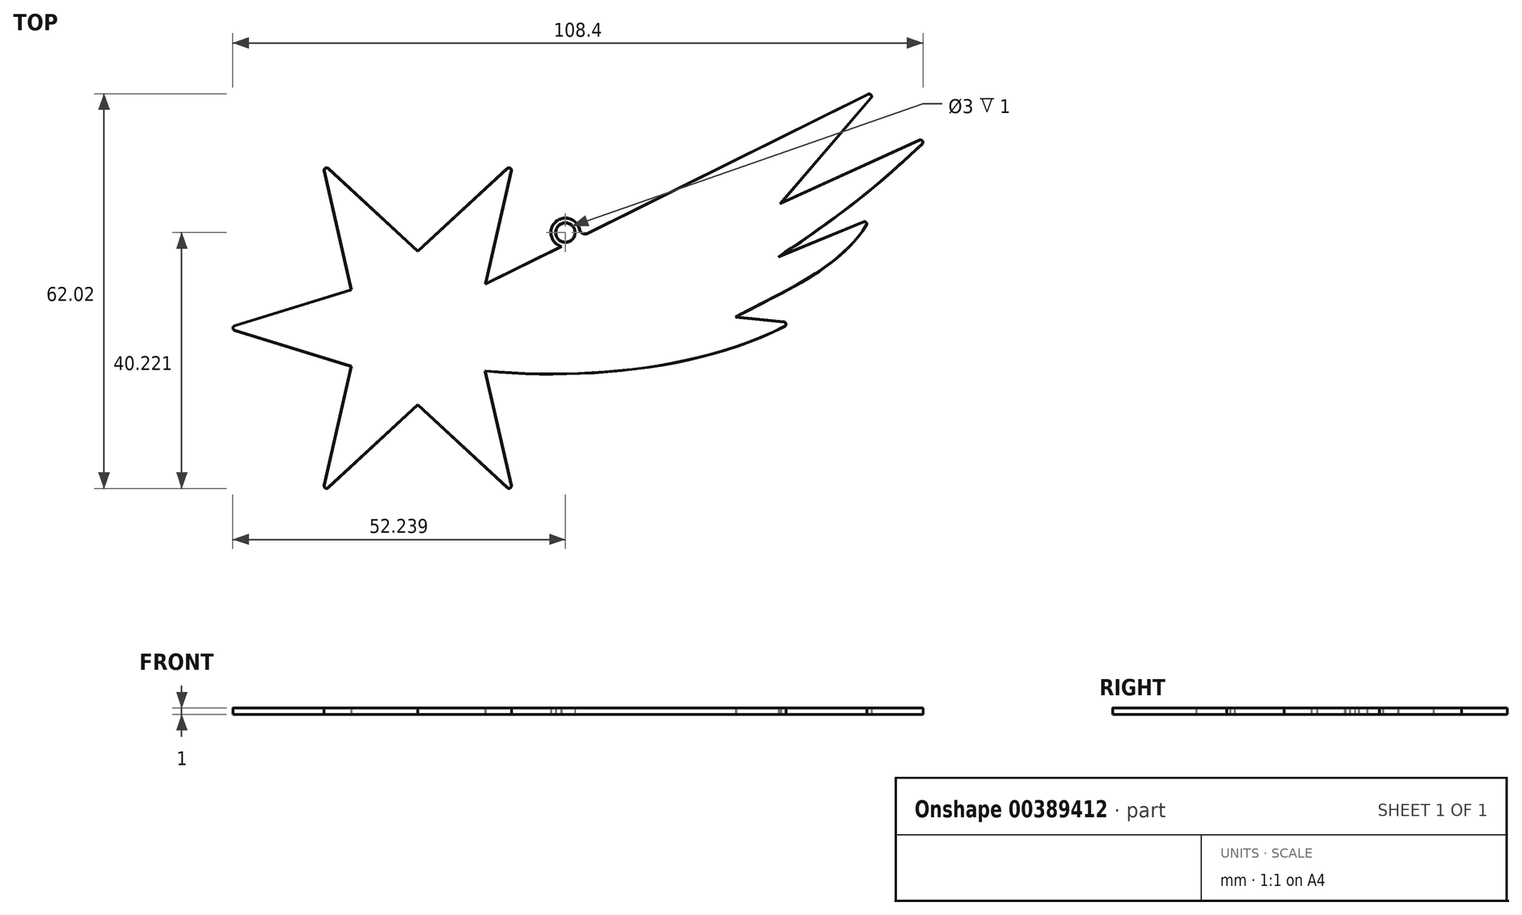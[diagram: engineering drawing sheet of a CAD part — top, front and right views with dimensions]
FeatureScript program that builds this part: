
annotation { "Feature Type Name" : "Feature", "Feature Type Description" : "" }
export const myFeature = defineFeature(function(context is Context, id is Id, definition is map)
    precondition{}
    {
        {
            var Q0;
            Q0=qCreatedBy(makeId("Top.planeOp"),FACE);
            var sketch = newSketch(context, id + "F0", { "sketchPlane" : qUnion([Q0])});
            skCircle(sketch, "E0.cCircle", {"center": v(0, 0) * mm, "radius": 30 * mm, "construction": true});
            skLineSegment(sketch, "E0.0", {"start": v(-30, 0) * mm, "end": v(-15, 25.98) * mm, "construction": true});
            skLineSegment(sketch, "E0.1", {"start": v(-15, 25.98) * mm, "end": v(15, 25.98) * mm, "construction": true});
            skLineSegment(sketch, "E0.2", {"start": v(15, 25.98) * mm, "end": v(30, 0) * mm, "construction": true});
            skLineSegment(sketch, "E0.3", {"start": v(30, 0) * mm, "end": v(15, -25.98) * mm, "construction": true});
            skLineSegment(sketch, "E0.4", {"start": v(15, -25.98) * mm, "end": v(-15, -25.98) * mm, "construction": true});
            skLineSegment(sketch, "E0.5", {"start": v(-15, -25.98) * mm, "end": v(-30, 0) * mm, "construction": true});
            skCircle(sketch, "E1.cCircle", {"center": v(0, 0) * mm, "radius": 12.09 * mm, "construction": true});
            skLineSegment(sketch, "E1.0", {"start": v(0, 12.09) * mm, "end": v(10.47, 6.04) * mm, "construction": true});
            skLineSegment(sketch, "E1.1", {"start": v(10.47, 6.04) * mm, "end": v(10.47, -6.04) * mm, "construction": true});
            skLineSegment(sketch, "E1.2", {"start": v(10.47, -6.04) * mm, "end": v(0, -12.09) * mm, "construction": true});
            skLineSegment(sketch, "E1.3", {"start": v(0, -12.09) * mm, "end": v(-10.47, -6.04) * mm, "construction": true});
            skLineSegment(sketch, "E1.4", {"start": v(-10.47, -6.04) * mm, "end": v(-10.47, 6.04) * mm, "construction": true});
            skLineSegment(sketch, "E1.5", {"start": v(-10.47, 6.04) * mm, "end": v(0, 12.09) * mm, "construction": true});
            skLineSegment(sketch, "E2", {"start": v(-15, 25.98) * mm, "end": v(-10.47, 6.04) * mm});
            skLineSegment(sketch, "E3", {"start": v(-30, 0) * mm, "end": v(-10.47, 6.04) * mm});
            skLineSegment(sketch, "E4", {"start": v(-30, 0) * mm, "end": v(-10.47, -6.04) * mm});
            skLineSegment(sketch, "E5", {"start": v(-10.47, -6.04) * mm, "end": v(-15, -25.98) * mm});
            skLineSegment(sketch, "E6", {"start": v(-15, -25.98) * mm, "end": v(0, -12.09) * mm});
            skLineSegment(sketch, "E7", {"start": v(0, -12.09) * mm, "end": v(15, -25.98) * mm});
            skLineSegment(sketch, "E8", {"start": v(15, -25.98) * mm, "end": v(10.47, -6.04) * mm});
            skLineSegment(sketch, "E9", {"start": v(10.47, -6.04) * mm, "end": v(30, 0) * mm});
            skLineSegment(sketch, "E10", {"start": v(30, 0) * mm, "end": v(10.47, 6.04) * mm});
            skLineSegment(sketch, "E11", {"start": v(10.47, 6.04) * mm, "end": v(15, 25.98) * mm});
            skLineSegment(sketch, "E12", {"start": v(15, 25.98) * mm, "end": v(0, 12.09) * mm});
            skLineSegment(sketch, "E13", {"start": v(0, 12.09) * mm, "end": v(-15, 25.98) * mm});
            skSolve(sketch);
        }
        {
            var Q0;
            Q0=qCreatedBy(makeId("Top.planeOp"),FACE);
            var sketch = newSketch(context, id + "F1", { "sketchPlane" : qUnion([Q0])});
            skLineSegment(sketch, "E14", {"start": v(7.39, 5.35) * mm, "end": v(72.49, 37.65) * mm});
            skFitSpline(sketch, "E15", {"points": [v(72.49, 37.65) * mm, v(57.07, 19.7) * mm], "startDerivative": vector(-15.42, -17.95) * mm, "endDerivative": vector(-15.42, -17.95) * mm});
            skFitSpline(sketch, "E16", {"points": [v(57.07, 19.7) * mm, v(80.89, 30.51) * mm], "startDerivative": vector(23.81, 10.81) * mm, "endDerivative": vector(23.81, 10.81) * mm});
            skFitSpline(sketch, "E17", {"points": [v(80.89, 30.51) * mm, v(57.07, 11.41) * mm], "startDerivative": vector(-25.7, -25.23) * mm, "endDerivative": vector(-26.86, -18.25) * mm});
            skFitSpline(sketch, "E18", {"points": [v(57.07, 11.41) * mm, v(71.1, 17.17) * mm], "startDerivative": vector(14.04, 5.75) * mm, "endDerivative": vector(14.04, 5.75) * mm});
            skFitSpline(sketch, "E19", {"points": [v(71.1, 17.17) * mm, v(50.05, 1.75) * mm], "startDerivative": vector(-12.49, -22.5) * mm, "endDerivative": vector(-25.34, -13.6) * mm});
            skFitSpline(sketch, "E20", {"points": [v(50.05, 1.75) * mm, v(58.82, 0.86) * mm], "startDerivative": vector(8.76, -0.9) * mm, "endDerivative": vector(8.76, -0.9) * mm});
            skFitSpline(sketch, "E21", {"points": [v(58.82, 0.86) * mm, v(7.78, -6.48) * mm], "startDerivative": vector(-41.96, -22.87) * mm, "endDerivative": vector(-51.14, 5.99) * mm});
            skLineSegment(sketch, "E22", {"start": v(7.78, -6.48) * mm, "end": v(7.39, 5.35) * mm});
            skSolve(sketch);
        }
        {
            var Q0;
            Q0=makeQuery(id+"F0.imprint","IMPRINT",FACE,{"disambiguationData":[TD([[makeQuery(id+"F0.imprint","IMPRINT",EDGE,{"derivedFrom":sQuery(id+"F0.wireOp",EDGE,"E2")}),1.0]])]});
            extrude(context, id + "F2", {"entities" : qUnion([Q0]), "depth" : 1 * mm});
        }
        {
            var Q0;
            Q0=qSketchRegion(id+"F1",true);
            extrude(context, id + "F3", {"entities" : qUnion([Q0]), "operationType" : NewBodyOperationType.ADD, "depth" : 1 * mm});
        }
        {
            var Q0;
            Q0=makeQuery(id+"F3.boolean.opBoolean","MERGE",FACE,{"derivedFrom":[makeQuery(id+"F2.opExtrude","CAP_FACE",FACE,{"disambiguationData":[OSD([sQuery(id+"F0.wireOp",EDGE,"E2"),sQuery(id+"F0.wireOp",EDGE,"E3"),sQuery(id+"F0.wireOp",EDGE,"E4"),sQuery(id+"F0.wireOp",EDGE,"E5"),sQuery(id+"F0.wireOp",EDGE,"E6"),sQuery(id+"F0.wireOp",EDGE,"E7"),sQuery(id+"F0.wireOp",EDGE,"E8"),sQuery(id+"F0.wireOp",EDGE,"E9"),sQuery(id+"F0.wireOp",EDGE,"E10"),sQuery(id+"F0.wireOp",EDGE,"E11"),sQuery(id+"F0.wireOp",EDGE,"E12"),sQuery(id+"F0.wireOp",EDGE,"E13")])],"isStart":true}),makeQuery(id+"F3.opExtrude","CAP_FACE",FACE,{"disambiguationData":[OSD([sQuery(id+"F1.wireOp",EDGE,"E14"),sQuery(id+"F1.wireOp",EDGE,"E15"),sQuery(id+"F1.wireOp",EDGE,"E16"),sQuery(id+"F1.wireOp",EDGE,"E17"),sQuery(id+"F1.wireOp",EDGE,"E18"),sQuery(id+"F1.wireOp",EDGE,"E19"),sQuery(id+"F1.wireOp",EDGE,"E20"),sQuery(id+"F1.wireOp",EDGE,"E21"),sQuery(id+"F1.wireOp",EDGE,"E22")])],"isStart":true})]});
            var sketch = newSketch(context, id + "F4", { "sketchPlane" : qUnion([Q0])});
            skCircle(sketch, "E23", {"center": v(23.19, -15.01) * mm, "radius": 2.3 * mm});
            skCircle(sketch, "E24", {"center": v(23.19, -15.01) * mm, "radius": 1.5 * mm});
            skSolve(sketch);
        }
        {
            var Q0;
            {var subQ4=sQuery(id+"F4.wireOp",EDGE,"E24");Q0=makeQuery(id+"F4.imprint","IMPRINT",FACE,{"disambiguationData":[TD([[makeQuery(id+"F4.imprint","IMPRINT",EDGE,{"derivedFrom":subQ4}),-1.0]])]});}
            extrude(context, id + "F5", {"entities" : qUnion([Q0]), "operationType" : NewBodyOperationType.ADD, "oppositeDirection" : true, "depth" : 1 * mm});
        }
        {
            var Q0;
            {var subQ0=sQuery(id+"F4.wireOp",EDGE,"E23");var subQ1=sQuery(id+"F1.wireOp",EDGE,"E14");Q0=makeQuery(id+"F5.opExtrude","SWEPT_EDGE",EDGE,{"disambiguationData":[OSD([subQ1,subQ0]),TDD([makeQuery(id+"F4.imprint","INTERSECT",VERTEX,{"disambiguationData":[OD(1.0)],"derivedFrom":[makeQuery(id+"F3.opExtrude","CAP_EDGE",EDGE,{"disambiguationData":[OSD([subQ1])],"isStart":true}),subQ0]})])]});}
            var Q1;
            {var subQ0=sQuery(id+"F4.wireOp",EDGE,"E23");var subQ1=sQuery(id+"F1.wireOp",EDGE,"E14");Q1=makeQuery(id+"F5.opExtrude","SWEPT_EDGE",EDGE,{"disambiguationData":[OSD([subQ1,subQ0]),TDD([makeQuery(id+"F4.imprint","INTERSECT",VERTEX,{"disambiguationData":[OD(0.0)],"derivedFrom":[makeQuery(id+"F3.opExtrude","CAP_EDGE",EDGE,{"disambiguationData":[OSD([subQ1])],"isStart":true}),subQ0]})])]});}
            fillet(context, id + "F6", {"entities" : qUnion([Q0, Q1]), "radius" : 0.86 * mm, "tangentPropagation" : true, "allowEdgeOverflow" : false});
        }
        {
            var Q0;
            Q0=makeQuery(id+"F2.opExtrude","SWEPT_EDGE",EDGE,{"disambiguationData":[OSD([sQuery(id+"F0.wireOp",EDGE,"E11"),sQuery(id+"F0.wireOp",EDGE,"E12")])]});
            var Q1;
            Q1=makeQuery(id+"F2.opExtrude","SWEPT_EDGE",EDGE,{"disambiguationData":[OSD([sQuery(id+"F0.wireOp",EDGE,"E2"),sQuery(id+"F0.wireOp",EDGE,"E13")])]});
            var Q2;
            Q2=makeQuery(id+"F2.opExtrude","SWEPT_EDGE",EDGE,{"disambiguationData":[OSD([sQuery(id+"F0.wireOp",EDGE,"E3"),sQuery(id+"F0.wireOp",EDGE,"E4")])]});
            var Q3;
            Q3=makeQuery(id+"F2.opExtrude","SWEPT_EDGE",EDGE,{"disambiguationData":[OSD([sQuery(id+"F0.wireOp",EDGE,"E5"),sQuery(id+"F0.wireOp",EDGE,"E6")])]});
            var Q4;
            Q4=makeQuery(id+"F2.opExtrude","SWEPT_EDGE",EDGE,{"disambiguationData":[OSD([sQuery(id+"F0.wireOp",EDGE,"E7"),sQuery(id+"F0.wireOp",EDGE,"E8")])]});
            var Q5;
            Q5=makeQuery(id+"F3.opExtrude","SWEPT_EDGE",EDGE,{"disambiguationData":[OSD([sQuery(id+"F1.wireOp",EDGE,"E14"),sQuery(id+"F1.wireOp",EDGE,"E15")])]});
            var Q6;
            Q6=makeQuery(id+"F3.opExtrude","SWEPT_EDGE",EDGE,{"disambiguationData":[OSD([sQuery(id+"F1.wireOp",EDGE,"E16"),sQuery(id+"F1.wireOp",EDGE,"E17")])]});
            var Q7;
            Q7=makeQuery(id+"F3.opExtrude","SWEPT_EDGE",EDGE,{"disambiguationData":[OSD([sQuery(id+"F1.wireOp",EDGE,"E18"),sQuery(id+"F1.wireOp",EDGE,"E19")])]});
            var Q8;
            Q8=makeQuery(id+"F3.opExtrude","SWEPT_EDGE",EDGE,{"disambiguationData":[OSD([sQuery(id+"F1.wireOp",EDGE,"E20"),sQuery(id+"F1.wireOp",EDGE,"E21")])]});
            fillet(context, id + "F7", {"entities" : qUnion([Q0, Q1, Q2, Q3, Q4, Q5, Q6, Q7, Q8]), "radius" : 0.4 * mm, "tangentPropagation" : true, "allowEdgeOverflow" : false});
        }
        {
            var Q0;
            {var subQ0=sQuery(id+"F1.wireOp",EDGE,"E14");Q0=makeQuery(id+"F5.boolean.opBoolean","MERGE",FACE,{"derivedFrom":[makeQuery(id+"F3.boolean.opBoolean","MERGE",FACE,{"derivedFrom":[makeQuery(id+"F2.opExtrude","CAP_FACE",FACE,{"disambiguationData":[OSD([sQuery(id+"F0.wireOp",EDGE,"E2"),sQuery(id+"F0.wireOp",EDGE,"E3"),sQuery(id+"F0.wireOp",EDGE,"E4"),sQuery(id+"F0.wireOp",EDGE,"E5"),sQuery(id+"F0.wireOp",EDGE,"E6"),sQuery(id+"F0.wireOp",EDGE,"E7"),sQuery(id+"F0.wireOp",EDGE,"E8"),sQuery(id+"F0.wireOp",EDGE,"E9"),sQuery(id+"F0.wireOp",EDGE,"E10"),sQuery(id+"F0.wireOp",EDGE,"E11"),sQuery(id+"F0.wireOp",EDGE,"E12"),sQuery(id+"F0.wireOp",EDGE,"E13")])],"isStart":false}),makeQuery(id+"F3.opExtrude","CAP_FACE",FACE,{"disambiguationData":[OSD([subQ0,sQuery(id+"F1.wireOp",EDGE,"E15"),sQuery(id+"F1.wireOp",EDGE,"E16"),sQuery(id+"F1.wireOp",EDGE,"E17"),sQuery(id+"F1.wireOp",EDGE,"E18"),sQuery(id+"F1.wireOp",EDGE,"E19"),sQuery(id+"F1.wireOp",EDGE,"E20"),sQuery(id+"F1.wireOp",EDGE,"E21"),sQuery(id+"F1.wireOp",EDGE,"E22")])],"isStart":false})]}),makeQuery(id+"F5.opExtrude","CAP_FACE",FACE,{"disambiguationData":[OSD([subQ0,sQuery(id+"F4.wireOp",EDGE,"E23"),sQuery(id+"F4.wireOp",EDGE,"E24")])],"isStart":false})]});}
            shell(context, id + "F8", {"entities" : qUnion([Q0]), "thickness" : 0.05 * mm});
        }
    });
